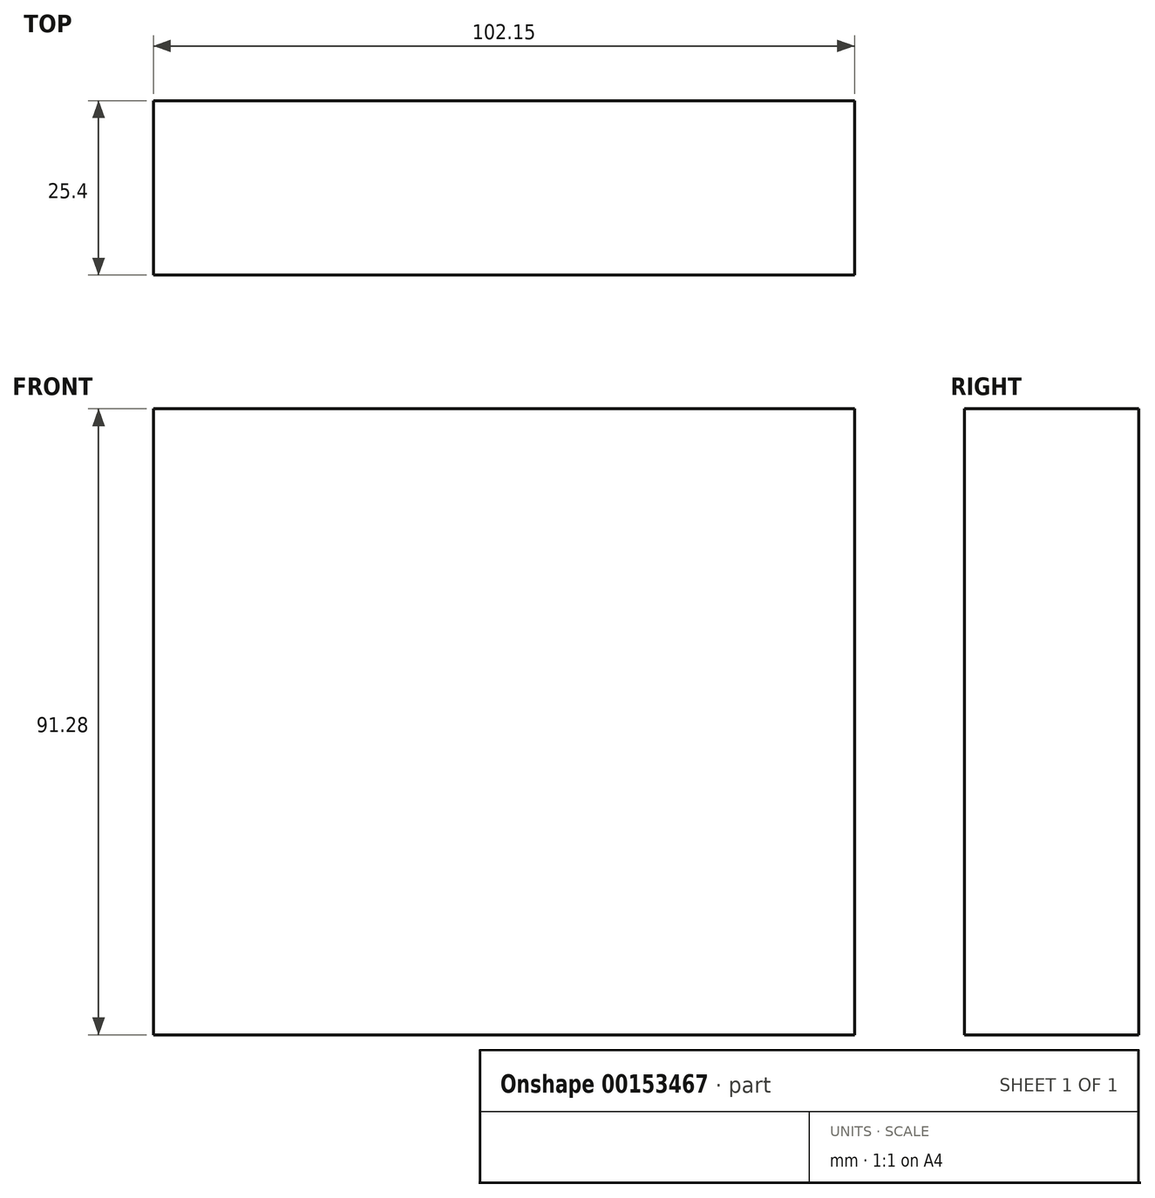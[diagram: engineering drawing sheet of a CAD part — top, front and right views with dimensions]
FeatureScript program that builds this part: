
annotation { "Feature Type Name" : "Feature", "Feature Type Description" : "" }
export const myFeature = defineFeature(function(context is Context, id is Id, definition is map)
    precondition{}
    {
        {
            var Q0;
            Q0=qCreatedBy(makeId("Front.planeOp"),FACE);
            var sketch = newSketch(context, id + "F0", { "sketchPlane" : qUnion([Q0])});
            skLineSegment(sketch, "E0.bottom", {"start": v(-58.52, 45.88) * mm, "end": v(43.63, 45.88) * mm});
            skLineSegment(sketch, "E0.top", {"start": v(-58.52, -45.4) * mm, "end": v(43.63, -45.4) * mm});
            skLineSegment(sketch, "E0.left", {"start": v(-58.52, 45.88) * mm, "end": v(-58.52, -45.4) * mm});
            skLineSegment(sketch, "E0.right", {"start": v(43.63, 45.88) * mm, "end": v(43.63, -45.4) * mm});
            skSolve(sketch);
        }
        {
            var Q0;
            Q0=makeQuery(id+"F0.imprint","IMPRINT",FACE,{"disambiguationData":[TD([[makeQuery(id+"F0.imprint","IMPRINT",EDGE,{"derivedFrom":sQuery(id+"F0.wireOp",EDGE,"E0.bottom")}),-1.0]])]});
            extrude(context, id + "F1", {"entities" : qUnion([Q0]), "depth" : 25.4 * mm});
        }
    });
